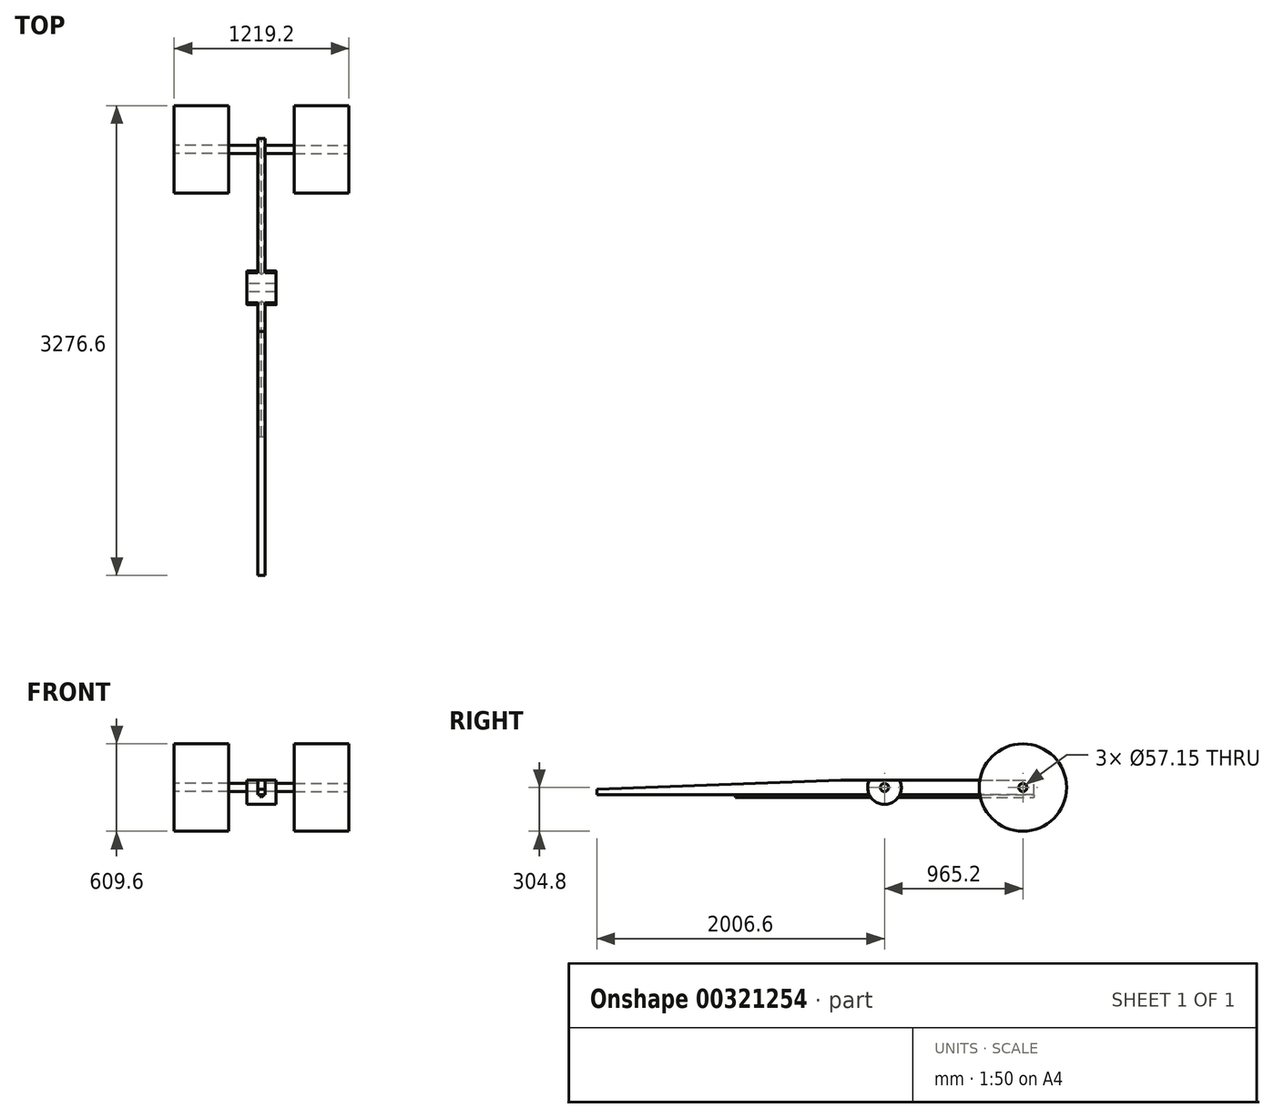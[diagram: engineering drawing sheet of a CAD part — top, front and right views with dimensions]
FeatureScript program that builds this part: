
annotation { "Feature Type Name" : "Feature", "Feature Type Description" : "" }
export const myFeature = defineFeature(function(context is Context, id is Id, definition is map)
    precondition{}
    {
        {
            var Q0;
            Q0=qCreatedBy(makeId("Right.planeOp"),FACE);
            var sketch = newSketch(context, id + "F0", { "sketchPlane" : qUnion([Q0])});
            skLineSegment(sketch, "E0.bottom", {"start": v(0, 0) * mm, "end": v(-3048, 0) * mm});
            skLineSegment(sketch, "E0.left", {"start": v(0, 0) * mm, "end": v(0, 101.6) * mm});
            skCircle(sketch, "E1", {"center": v(-76.2, 50.8) * mm, "radius": 28.58 * mm});
            skPoint(sketch, "E1.centerSnap0", {"position": v(0, 50.8) * mm});
            skCircle(sketch, "E2", {"center": v(-1041.4, 50.8) * mm, "radius": 117.48 * mm});
            skCircle(sketch, "E3", {"center": v(-1041.4, 50.8) * mm, "radius": 28.58 * mm});
            skLineSegment(sketch, "E4", {"start": v(-1346.2, 101.6) * mm, "end": v(-1346.2, 0) * mm});
            skLineSegment(sketch, "E5", {"start": v(-1346.2, 101.6) * mm, "end": v(-3048, 38.1) * mm});
            skLineSegment(sketch, "E6", {"start": v(-1346.2, 101.6) * mm, "end": v(0, 101.6) * mm});
            skLineSegment(sketch, "E7", {"start": v(-3048, 0) * mm, "end": v(-3048, 38.1) * mm});
            skSolve(sketch);
        }
        {
            var Q0;
            Q0=makeQuery(id+"F0.imprint","IMPRINT",FACE,{"disambiguationData":[TD([[makeQuery(id+"F0.imprint","IMPRINT",EDGE,{"derivedFrom":sQuery(id+"F0.wireOp",EDGE,"E0.bottom")}),-1.0]])]});
            var Q1;
            {var subQ0=sQuery(id+"F0.wireOp",EDGE,"E0.left");Q1=makeQuery(id+"F0.imprint","IMPRINT",FACE,{"disambiguationData":[TD([[makeQuery(id+"F0.imprint","IMPRINT",EDGE,{"derivedFrom":subQ0}),1.0]])]});}
            var Q2;
            Q2=makeQuery(id+"F0.imprint","IMPRINT",FACE,{"disambiguationData":[TD([[makeQuery(id+"F0.imprint","IMPRINT",EDGE,{"derivedFrom":sQuery(id+"F0.wireOp",EDGE,"E3")}),-1.0]])]});
            extrude(context, id + "F1", {"entities" : qUnion([Q0, Q1, Q2]), "endBound" : BoundingType.SYMMETRIC, "depth" : 50.8 * mm});
        }
        {
            var Q0;
            Q0=makeQuery(id+"F0.imprint","IMPRINT",FACE,{"disambiguationData":[TD([[makeQuery(id+"F0.imprint","IMPRINT",EDGE,{"derivedFrom":sQuery(id+"F0.wireOp",EDGE,"E2")}),1.0]])]});
            var Q1;
            {var subQ0=sQuery(id+"F0.wireOp",EDGE,"E2");var subQ1=sQuery(id+"F0.wireOp",EDGE,"E0.top");var subQ2=makeQuery(id+"F0.imprint","INTERSECT",VERTEX,{"disambiguationData":[OD(0.0)],"derivedFrom":[subQ1,subQ0]});Q1=makeQuery(id+"F0.imprint","IMPRINT",FACE,{"disambiguationData":[TD([[makeQuery(id+"F0.imprint","IMPRINT",EDGE,{"disambiguationData":[TD([[subQ2,-1.0]])],"derivedFrom":subQ1}),-1.0]])]});}
            var Q2;
            {var subQ0=sQuery(id+"F0.wireOp",EDGE,"E2");var subQ1=sQuery(id+"F0.wireOp",EDGE,"E0.bottom");var subQ2=makeQuery(id+"F0.imprint","INTERSECT",VERTEX,{"disambiguationData":[OD(0.0)],"derivedFrom":[subQ1,subQ0]});Q2=makeQuery(id+"F0.imprint","IMPRINT",FACE,{"disambiguationData":[TD([[makeQuery(id+"F0.imprint","IMPRINT",EDGE,{"disambiguationData":[TD([[subQ2,-1.0]])],"derivedFrom":subQ1}),1.0]])]});}
            var Q3;
            {var subQ0=sQuery(id+"F0.wireOp",EDGE,"E6");var subQ1=sQuery(id+"F0.wireOp",EDGE,"E2");var subQ2=makeQuery(id+"F0.imprint","INTERSECT",VERTEX,{"disambiguationData":[OD(0.0)],"derivedFrom":[subQ1,subQ0]});Q3=makeQuery(id+"F0.imprint","IMPRINT",FACE,{"disambiguationData":[TD([[makeQuery(id+"F0.imprint","IMPRINT",EDGE,{"disambiguationData":[TD([[subQ2,1.0]])],"derivedFrom":subQ1}),1.0]])]});}
            extrude(context, id + "F2", {"entities" : qUnion([Q0, Q1, Q2, Q3]), "endBound" : BoundingType.SYMMETRIC, "depth" : 203.2 * mm});
        }
        {
            var Q0;
            Q0=makeQuery(id+"F0.imprint","IMPRINT",FACE,{"disambiguationData":[TD([[makeQuery(id+"F0.imprint","IMPRINT",EDGE,{"derivedFrom":sQuery(id+"F0.wireOp",EDGE,"E1")}),1.0]])]});
            extrude(context, id + "F3", {"entities" : qUnion([Q0]), "operationType" : NewBodyOperationType.ADD, "endBound" : BoundingType.SYMMETRIC, "depth" : 1219.2 * mm});
        }
        {
            var Q0;
            Q0=makeQuery(id+"F1.opExtrude","SWEPT_FACE",FACE,{"disambiguationData":[OSD([sQuery(id+"F0.wireOp",EDGE,"E0.left")])]});
            var sketch = newSketch(context, id + "F4", { "sketchPlane" : qUnion([Q0])});
            skLineSegment(sketch, "E8", {"start": v(-17.02, 0) * mm, "end": v(0, -17.24) * mm});
            skLineSegment(sketch, "E9", {"start": v(0, -17.24) * mm, "end": v(17.47, 0) * mm});
            skLineSegment(sketch, "E10", {"start": v(-17.02, 0) * mm, "end": v(17.47, 0) * mm});
            skSolve(sketch);
        }
        {
            var Q0;
            Q0=makeQuery(id+"F4.imprint","IMPRINT",FACE,{"disambiguationData":[TD([[makeQuery(id+"F4.imprint","IMPRINT",EDGE,{"derivedFrom":sQuery(id+"F4.wireOp",EDGE,"E8")}),1.0]])]});
            extrude(context, id + "F5", {"entities" : qUnion([Q0]), "operationType" : NewBodyOperationType.ADD, "oppositeDirection" : true, "depth" : 2082.8 * mm});
        }
        {
            var Q0;
            Q0=makeQuery(id+"F3.opExtrude","CAP_FACE",FACE,{"disambiguationData":[OSD([sQuery(id+"F0.wireOp",EDGE,"E1")])],"isStart":false});
            var sketch = newSketch(context, id + "F6", { "sketchPlane" : qUnion([Q0])});
            skCircle(sketch, "E11", {"center": v(-76.2, 50.8) * mm, "radius": 304.8 * mm});
            skSolve(sketch);
        }
        {
            var Q0;
            Q0=makeQuery(id+"F6.imprint","IMPRINT",FACE,{"disambiguationData":[TD([[makeQuery(id+"F6.imprint","IMPRINT",EDGE,{"derivedFrom":sQuery(id+"F6.wireOp",EDGE,"E11")}),1.0]])]});
            extrude(context, id + "F7", {"entities" : qUnion([Q0]), "oppositeDirection" : true, "depth" : 381 * mm});
        }
        {
            var Q0;
            Q0=makeQuery(id+"F7.opExtrude","SWEPT_BODY",BODY,{"disambiguationData":[OSD([sQuery(id+"F0.wireOp",EDGE,"E1"),sQuery(id+"F6.wireOp",EDGE,"E11")])]});
            var Q1;
            Q1=qCreatedBy(makeId("Right.planeOp"),FACE);
            mirror(context, id + "F8", {"entities" : qUnion([Q0]), "mirrorPlane" : qUnion([Q1])});
        }
    });
